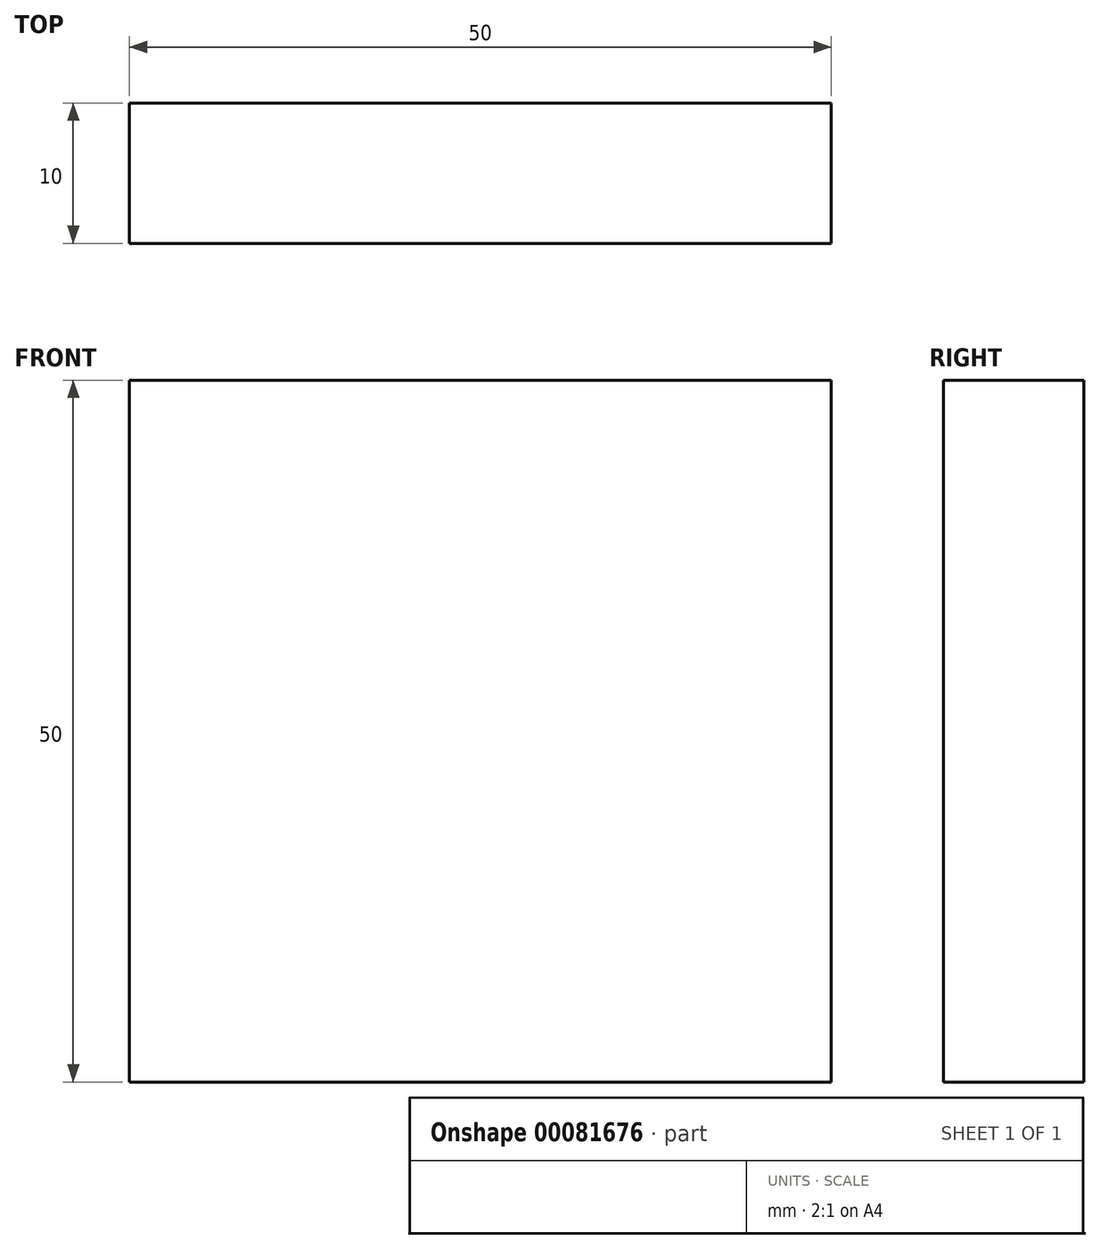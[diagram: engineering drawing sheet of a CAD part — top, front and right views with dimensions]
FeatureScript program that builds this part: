
annotation { "Feature Type Name" : "Feature", "Feature Type Description" : "" }
export const myFeature = defineFeature(function(context is Context, id is Id, definition is map)
    precondition{}
    {
        {
            var Q0;
            Q0=qCreatedBy(makeId("Front.planeOp"),FACE);
            var sketch = newSketch(context, id + "F0", { "sketchPlane" : qUnion([Q0])});
            skLineSegment(sketch, "E0.bottom", {"start": v(-83.26, -5.18) * mm, "end": v(-33.26, -5.18) * mm});
            skLineSegment(sketch, "E0.top", {"start": v(-83.26, -55.18) * mm, "end": v(-33.26, -55.18) * mm});
            skLineSegment(sketch, "E0.left", {"start": v(-83.26, -5.18) * mm, "end": v(-83.26, -55.18) * mm});
            skLineSegment(sketch, "E0.right", {"start": v(-33.26, -5.18) * mm, "end": v(-33.26, -55.18) * mm});
            skSolve(sketch);
        }
        {
            var Q0;
            Q0 = qSketchRegion(id + "F0", true);
            extrude(context, id + "F1", {"entities" : qUnion([Q0]), "depth" : 10 * mm});
        }
    });
